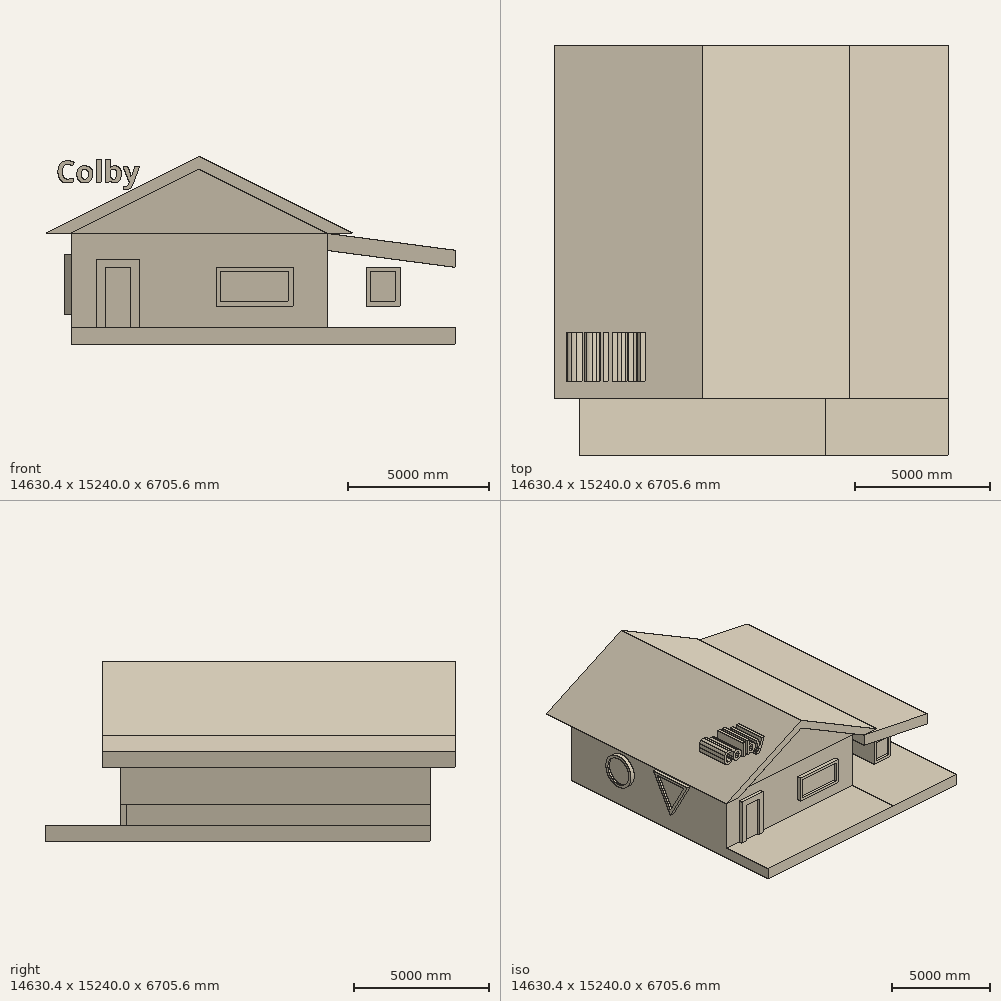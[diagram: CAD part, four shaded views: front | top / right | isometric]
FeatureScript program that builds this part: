
annotation { "Feature Type Name" : "Feature", "Feature Type Description" : "" }
export const myFeature = defineFeature(function(context is Context, id is Id, definition is map)
    precondition{}
    {
        {
            var Q0;
            Q0=qCreatedBy(makeId("Front.planeOp"),FACE);
            var sketch = newSketch(context, id + "F0", { "sketchPlane" : qUnion([Q0])});
            skLineSegment(sketch, "E0", {"start": v(0, 0) * mm, "end": v(-4572, 0) * mm});
            skLineSegment(sketch, "E1", {"start": v(0, 0) * mm, "end": v(4572, 0) * mm});
            skLineSegment(sketch, "E2", {"start": v(0, 0) * mm, "end": v(0, 2286) * mm});
            skLineSegment(sketch, "E3", {"start": v(-4572, 0) * mm, "end": v(0, 2286) * mm});
            skLineSegment(sketch, "E4", {"start": v(4572, 0) * mm, "end": v(0, 2286) * mm});
            skLineSegment(sketch, "E5", {"start": v(-4572, 0) * mm, "end": v(-5486.4, 0) * mm});
            skLineSegment(sketch, "E6", {"start": v(0, 2286) * mm, "end": v(0, 2743.2) * mm});
            skLineSegment(sketch, "E7", {"start": v(4572, 0) * mm, "end": v(5486.4, 0) * mm});
            skLineSegment(sketch, "E8", {"start": v(5486.4, 0) * mm, "end": v(0, 2743.2) * mm});
            skLineSegment(sketch, "E9", {"start": v(-5486.4, 0) * mm, "end": v(0, 2743.2) * mm});
            skLineSegment(sketch, "E10", {"start": v(-4572, 0) * mm, "end": v(-4572, -3352.8) * mm});
            skLineSegment(sketch, "E11", {"start": v(4572, 0) * mm, "end": v(4572, -3352.8) * mm});
            skLineSegment(sketch, "E12", {"start": v(4572, -3352.8) * mm, "end": v(-4572, -3352.8) * mm});
            skLineSegment(sketch, "E13", {"start": v(-4572, -3352.8) * mm, "end": v(-4572, -3962.4) * mm});
            skLineSegment(sketch, "E14", {"start": v(4572, -3352.8) * mm, "end": v(4572, -3962.4) * mm});
            skLineSegment(sketch, "E15", {"start": v(4572, -3962.4) * mm, "end": v(-4572, -3962.4) * mm});
            skLineSegment(sketch, "E16", {"start": v(-3352.8, -3352.8) * mm, "end": v(-3352.8, -1219.2) * mm});
            skLineSegment(sketch, "E17", {"start": v(-3352.8, -1219.2) * mm, "end": v(-2438.4, -1219.2) * mm});
            skLineSegment(sketch, "E18", {"start": v(-2438.4, -1219.2) * mm, "end": v(-2438.4, -3352.8) * mm});
            skLineSegment(sketch, "E19.bottom", {"start": v(609.6, -1219.2) * mm, "end": v(3352.8, -1219.2) * mm});
            skLineSegment(sketch, "E19.top", {"start": v(609.6, -2590.8) * mm, "end": v(3352.8, -2590.8) * mm});
            skLineSegment(sketch, "E19.left", {"start": v(609.6, -1219.2) * mm, "end": v(609.6, -2590.8) * mm});
            skLineSegment(sketch, "E19.right", {"start": v(3352.8, -1219.2) * mm, "end": v(3352.8, -2590.8) * mm});
            skLineSegment(sketch, "E20.0", {"start": v(762, -1371.6) * mm, "end": v(3200.4, -1371.6) * mm});
            skLineSegment(sketch, "E20.1", {"start": v(762, -1371.6) * mm, "end": v(762, -2438.4) * mm});
            skLineSegment(sketch, "E20.2", {"start": v(762, -2438.4) * mm, "end": v(3200.4, -2438.4) * mm});
            skLineSegment(sketch, "E20.3", {"start": v(3200.4, -1371.6) * mm, "end": v(3200.4, -2438.4) * mm});
            skLineSegment(sketch, "E21.0", {"start": v(-2133.6, -914.4) * mm, "end": v(-2133.6, -3352.8) * mm});
            skLineSegment(sketch, "E21.1", {"start": v(-3657.6, -914.4) * mm, "end": v(-2133.6, -914.4) * mm});
            skLineSegment(sketch, "E21.2", {"start": v(-3657.6, -3352.8) * mm, "end": v(-3657.6, -914.4) * mm});
            skLineSegment(sketch, "E22", {"start": v(4572, 0) * mm, "end": v(9144, -603.27) * mm});
            skLineSegment(sketch, "E23", {"start": v(9144, -603.27) * mm, "end": v(9144, -3346.47) * mm});
            skLineSegment(sketch, "E24", {"start": v(9144, -3346.47) * mm, "end": v(4572, -3352.8) * mm});
            skLineSegment(sketch, "E25", {"start": v(4572, -3962.4) * mm, "end": v(9144, -3962.4) * mm});
            skLineSegment(sketch, "E26", {"start": v(9144, -3962.4) * mm, "end": v(9144, -3346.47) * mm});
            skLineSegment(sketch, "E27", {"start": v(4572, 0) * mm, "end": v(4572, -609.6) * mm});
            skLineSegment(sketch, "E28", {"start": v(9144, -603.27) * mm, "end": v(9144, -1212.87) * mm});
            skLineSegment(sketch, "E29", {"start": v(4572, -609.6) * mm, "end": v(9144, -1212.87) * mm});
            skLineSegment(sketch, "E30.bottom", {"start": v(5951.04, -1219.2) * mm, "end": v(7170.24, -1219.2) * mm});
            skLineSegment(sketch, "E30.top", {"start": v(5951.04, -2590.8) * mm, "end": v(7170.24, -2590.8) * mm});
            skLineSegment(sketch, "E30.left", {"start": v(5951.04, -1219.2) * mm, "end": v(5951.04, -2590.8) * mm});
            skLineSegment(sketch, "E30.right", {"start": v(7170.24, -1219.2) * mm, "end": v(7170.24, -2590.8) * mm});
            skLineSegment(sketch, "E31.0", {"start": v(6103.44, -1371.6) * mm, "end": v(6103.44, -2438.4) * mm});
            skLineSegment(sketch, "E31.1", {"start": v(6103.44, -1371.6) * mm, "end": v(7017.84, -1371.6) * mm});
            skLineSegment(sketch, "E31.2", {"start": v(7017.84, -1371.6) * mm, "end": v(7017.84, -2438.4) * mm});
            skLineSegment(sketch, "E31.3", {"start": v(6103.44, -2438.4) * mm, "end": v(7017.84, -2438.4) * mm});
            skText(sketch, "E32", { "text": "Colby", "fontName": "OpenSans-Bold.ttf"});
            const initialGuessF0  = {"E32": [-5.10518, 1.80998, 1, 0, 0.77946]};
            skSetInitialGuess(sketch, initialGuessF0);
            skSolve(sketch);
        }
        {
            var Q0;
            Q0=makeQuery(id+"F0.imprint","IMPRINT",FACE,{"disambiguationData":[TD([[makeQuery(id+"F0.imprint","IMPRINT",EDGE,{"derivedFrom":sQuery(id+"F0.wireOp",EDGE,"E4")}),-1.0]])]});
            var Q1;
            Q1=makeQuery(id+"F0.imprint","IMPRINT",FACE,{"disambiguationData":[TD([[makeQuery(id+"F0.imprint","IMPRINT",EDGE,{"derivedFrom":sQuery(id+"F0.wireOp",EDGE,"E3")}),1.0]])]});
            var Q2;
            Q2=makeQuery(id+"F0.imprint","IMPRINT",FACE,{"disambiguationData":[TD([[makeQuery(id+"F0.imprint","IMPRINT",EDGE,{"derivedFrom":sQuery(id+"F0.wireOp",EDGE,"E22")}),-1.0]])]});
            extrude(context, id + "F1", {"entities" : qUnion([Q0, Q1, Q2]), "depth" : 914.4 * mm, "offsetDistance" : 30.48 * mm, "hasSecondDirection" : true, "secondDirectionOppositeDirection" : true, "secondDirectionDepth" : 12192 * mm});
        }
        {
            var Q0;
            Q0=makeQuery(id+"F0.imprint","IMPRINT",FACE,{"disambiguationData":[TD([[makeQuery(id+"F0.imprint","IMPRINT",EDGE,{"derivedFrom":sQuery(id+"F0.wireOp",EDGE,"E0")}),1.0]])]});
            var Q1;
            {var subQ0=sQuery(id+"F0.wireOp",EDGE,"E16");Q1=makeQuery(id+"F0.imprint","IMPRINT",FACE,{"disambiguationData":[TD([[makeQuery(id+"F0.imprint","IMPRINT",EDGE,{"derivedFrom":subQ0}),1.0]])]});}
            var Q2;
            {var subQ0=sQuery(id+"F0.wireOp",EDGE,"E16");Q2=makeQuery(id+"F0.imprint","IMPRINT",FACE,{"disambiguationData":[TD([[makeQuery(id+"F0.imprint","IMPRINT",EDGE,{"derivedFrom":subQ0}),-1.0]])]});}
            var Q3;
            Q3=makeQuery(id+"F0.imprint","IMPRINT",FACE,{"disambiguationData":[TD([[makeQuery(id+"F0.imprint","IMPRINT",EDGE,{"derivedFrom":sQuery(id+"F0.wireOp",EDGE,"E20.0")}),-1.0]])]});
            var Q4;
            Q4=makeQuery(id+"F0.imprint","IMPRINT",FACE,{"disambiguationData":[TD([[makeQuery(id+"F0.imprint","IMPRINT",EDGE,{"derivedFrom":sQuery(id+"F0.wireOp",EDGE,"E19.bottom")}),-1.0]])]});
            var Q5;
            Q5=makeQuery(id+"F0.imprint","IMPRINT",FACE,{"disambiguationData":[TD([[makeQuery(id+"F0.imprint","IMPRINT",EDGE,{"derivedFrom":sQuery(id+"F0.wireOp",EDGE,"E11")}),1.0]])]});
            var Q6;
            Q6=makeQuery(id+"F0.imprint","IMPRINT",FACE,{"disambiguationData":[TD([[makeQuery(id+"F0.imprint","IMPRINT",EDGE,{"derivedFrom":sQuery(id+"F0.wireOp",EDGE,"E30.bottom")}),-1.0]])]});
            var Q7;
            Q7=makeQuery(id+"F0.imprint","IMPRINT",FACE,{"disambiguationData":[TD([[makeQuery(id+"F0.imprint","IMPRINT",EDGE,{"derivedFrom":sQuery(id+"F0.wireOp",EDGE,"E31.0")}),1.0]])]});
            extrude(context, id + "F2", {"entities" : qUnion([Q0, Q1, Q2, Q3, Q4, Q5, Q6, Q7]), "operationType" : NewBodyOperationType.ADD, "depth" : 30.48 * mm, "offsetDistance" : 30.48 * mm, "hasSecondDirection" : true, "secondDirectionOppositeDirection" : true, "secondDirectionDepth" : 11277.6 * mm});
        }
        {
            var Q0;
            {var subQ6=sQuery(id+"F0.wireOp",EDGE,"E13");Q0=makeQuery(id+"F0.imprint","IMPRINT",FACE,{"disambiguationData":[TD([[makeQuery(id+"F0.imprint","IMPRINT",EDGE,{"derivedFrom":subQ6}),1.0]])]});}
            var Q1;
            Q1=makeQuery(id+"F0.imprint","IMPRINT",FACE,{"disambiguationData":[TD([[makeQuery(id+"F0.imprint","IMPRINT",EDGE,{"derivedFrom":sQuery(id+"F0.wireOp",EDGE,"E14")}),1.0]])]});
            extrude(context, id + "F3", {"entities" : qUnion([Q0, Q1]), "operationType" : NewBodyOperationType.ADD, "depth" : 3048 * mm, "offsetDistance" : 30.48 * mm, "hasSecondDirection" : true, "secondDirectionOppositeDirection" : true, "secondDirectionDepth" : 11277.6 * mm});
        }
        {
            var Q0;
            Q0=makeQuery(id+"F0.imprint","IMPRINT",FACE,{"disambiguationData":[TD([[makeQuery(id+"F0.imprint","IMPRINT",EDGE,{"derivedFrom":sQuery(id+"F0.wireOp",EDGE,"E0")}),-1.0]])]});
            var Q1;
            Q1=makeQuery(id+"F0.imprint","IMPRINT",FACE,{"disambiguationData":[TD([[makeQuery(id+"F0.imprint","IMPRINT",EDGE,{"derivedFrom":sQuery(id+"F0.wireOp",EDGE,"E1")}),1.0]])]});
            extrude(context, id + "F4", {"entities" : qUnion([Q0, Q1]), "depth" : 457.2 * mm, "offsetDistance" : 30.48 * mm, "hasSecondDirection" : true, "secondDirectionOppositeDirection" : true, "secondDirectionDepth" : 11734.8 * mm});
        }
        {
            var Q0;
            {var subQ0=sQuery(id+"F0.wireOp",EDGE,"E16");Q0=makeQuery(id+"F0.imprint","IMPRINT",FACE,{"disambiguationData":[TD([[makeQuery(id+"F0.imprint","IMPRINT",EDGE,{"derivedFrom":subQ0}),-1.0]])]});}
            var Q1;
            Q1=makeQuery(id+"F0.imprint","IMPRINT",FACE,{"disambiguationData":[TD([[makeQuery(id+"F0.imprint","IMPRINT",EDGE,{"derivedFrom":sQuery(id+"F0.wireOp",EDGE,"E20.0")}),-1.0]])]});
            var Q2;
            Q2=makeQuery(id+"F0.imprint","IMPRINT",FACE,{"disambiguationData":[TD([[makeQuery(id+"F0.imprint","IMPRINT",EDGE,{"derivedFrom":sQuery(id+"F0.wireOp",EDGE,"E31.0")}),1.0]])]});
            extrude(context, id + "F5", {"entities" : qUnion([Q0, Q1, Q2]), "operationType" : NewBodyOperationType.ADD, "depth" : 121.92 * mm, "offsetDistance" : 30.48 * mm});
        }
        {
            var Q0;
            {var subQ0=sQuery(id+"F0.wireOp",EDGE,"E16");Q0=makeQuery(id+"F0.imprint","IMPRINT",FACE,{"disambiguationData":[TD([[makeQuery(id+"F0.imprint","IMPRINT",EDGE,{"derivedFrom":subQ0}),1.0]])]});}
            var Q1;
            Q1=makeQuery(id+"F0.imprint","IMPRINT",FACE,{"disambiguationData":[TD([[makeQuery(id+"F0.imprint","IMPRINT",EDGE,{"derivedFrom":sQuery(id+"F0.wireOp",EDGE,"E19.bottom")}),-1.0]])]});
            var Q2;
            Q2=makeQuery(id+"F0.imprint","IMPRINT",FACE,{"disambiguationData":[TD([[makeQuery(id+"F0.imprint","IMPRINT",EDGE,{"derivedFrom":sQuery(id+"F0.wireOp",EDGE,"E30.bottom")}),-1.0]])]});
            extrude(context, id + "F6", {"entities" : qUnion([Q0, Q1, Q2]), "operationType" : NewBodyOperationType.ADD, "depth" : 243.84 * mm, "offsetDistance" : 30.48 * mm});
        }
        {
            var Q0;
            Q0=makeQuery(id+"F3.boolean.opBoolean","MERGE",FACE,{"derivedFrom":[makeQuery(id+"F2.opExtrude","SWEPT_FACE",FACE,{"disambiguationData":[OSD([sQuery(id+"F0.wireOp",EDGE,"E10")])]}),makeQuery(id+"F3.opExtrude","SWEPT_FACE",FACE,{"disambiguationData":[OSD([sQuery(id+"F0.wireOp",EDGE,"E13")])]})]});
            var sketch = newSketch(context, id + "F7", { "sketchPlane" : qUnion([Q0])});
            skCircle(sketch, "E33", {"center": v(-7623.18, -1828.8) * mm, "radius": 914.4 * mm});
            skCircle(sketch, "E34.cCircle", {"center": v(-3826.86, -1468.32) * mm, "radius": 713.64 * mm, "construction": true});
            skLineSegment(sketch, "E34.0", {"start": v(-5062.92, -754.68) * mm, "end": v(-2590.8, -754.68) * mm});
            skLineSegment(sketch, "E34.1", {"start": v(-2590.8, -754.68) * mm, "end": v(-3826.86, -2895.6) * mm});
            skLineSegment(sketch, "E34.2", {"start": v(-3826.86, -2895.6) * mm, "end": v(-5062.92, -754.68) * mm});
            skPoint(sketch, "E34.0.midPoint", {"position": v(-3826.86, -754.68) * mm});
            skCircle(sketch, "E35.0", {"center": v(-7623.18, -1828.8) * mm, "radius": 762 * mm});
            skLineSegment(sketch, "E36.0", {"start": v(-3826.86, -2590.8) * mm, "end": v(-4798.96, -907.08) * mm});
            skLineSegment(sketch, "E36.1", {"start": v(-2854.76, -907.08) * mm, "end": v(-3826.86, -2590.8) * mm});
            skLineSegment(sketch, "E36.2", {"start": v(-4798.96, -907.08) * mm, "end": v(-2854.76, -907.08) * mm});
            skSolve(sketch);
        }
        {
            var Q0;
            Q0 = qSketchRegion(id + "F7", true);
            extrude(context, id + "F8", {"entities" : qUnion([Q0]), "operationType" : NewBodyOperationType.ADD, "depth" : 243.84 * mm, "offsetDistance" : 30.48 * mm});
        }
        {
            var Q0;
            Q0=makeQuery(id+"F7.imprint","IMPRINT",FACE,{"disambiguationData":[TD([[makeQuery(id+"F7.imprint","IMPRINT",EDGE,{"derivedFrom":sQuery(id+"F7.wireOp",EDGE,"E35.0")}),1.0]])]});
            var Q1;
            Q1=makeQuery(id+"F7.imprint","IMPRINT",FACE,{"disambiguationData":[TD([[makeQuery(id+"F7.imprint","IMPRINT",EDGE,{"derivedFrom":sQuery(id+"F7.wireOp",EDGE,"E36.0")}),-1.0]])]});
            extrude(context, id + "F9", {"entities" : qUnion([Q0, Q1]), "operationType" : NewBodyOperationType.ADD, "depth" : 121.92 * mm, "offsetDistance" : 30.48 * mm});
        }
        {
            var Q0;
            Q0=makeQuery(id+"F0.imprint","IMPRINT",FACE,{"disambiguationData":[TD([[makeQuery(id+"F0.imprint","IMPRINT",EDGE,{"derivedFrom":sQuery(id+"F0.wireOp",EDGE,"E32.sketch_text.stroke-60")}),-1.0]])]});
            var Q1;
            Q1=makeQuery(id+"F0.imprint","IMPRINT",FACE,{"disambiguationData":[TD([[makeQuery(id+"F0.imprint","IMPRINT",EDGE,{"derivedFrom":sQuery(id+"F0.wireOp",EDGE,"E32.sketch_text.stroke-37")}),-1.0]])]});
            var Q2;
            Q2=makeQuery(id+"F0.imprint","IMPRINT",FACE,{"disambiguationData":[TD([[makeQuery(id+"F0.imprint","IMPRINT",EDGE,{"derivedFrom":sQuery(id+"F0.wireOp",EDGE,"E32.sketch_text.stroke-33")}),-1.0]])]});
            var Q3;
            Q3=makeQuery(id+"F0.imprint","IMPRINT",FACE,{"disambiguationData":[TD([[makeQuery(id+"F0.imprint","IMPRINT",EDGE,{"derivedFrom":sQuery(id+"F0.wireOp",EDGE,"E32.sketch_text.stroke-15")}),-1.0]])]});
            var Q4;
            Q4=makeQuery(id+"F0.imprint","IMPRINT",FACE,{"disambiguationData":[TD([[makeQuery(id+"F0.imprint","IMPRINT",EDGE,{"derivedFrom":sQuery(id+"F0.wireOp",EDGE,"E32.sketch_text.stroke-0")}),-1.0]])]});
            extrude(context, id + "F10", {"entities" : qUnion([Q0, Q1, Q2, Q3, Q4]), "depth" : 304.8 * mm, "offsetDistance" : 30.48 * mm, "hasSecondDirection" : true, "secondDirectionOppositeDirection" : true, "secondDirectionDepth" : 1524 * mm});
        }
    });
